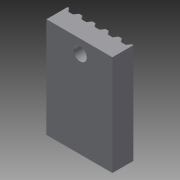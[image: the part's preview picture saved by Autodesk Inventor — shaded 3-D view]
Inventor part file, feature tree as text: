
AUTODESK INVENTOR PART (.ipt)
format: ipt  version: 2015 SP1 (Build 190203100, 203)  size: 166,912 bytes
history: native  units: in
note: dims shown in document units (in); Inventor stores cm internally (conversion verified against a paired STEP export)
features: extrude x4, sketch x4, projected_geometry x1
ambient origin geometry x8: Origin, YZ Plane, XZ Plane, XY Plane, X Axis, Y Axis, Z Axis, Center Point
bodies: Body1 (feature_tree)
feature tree (9):
  extrude  "Extrusion2"  Depth=0.1575in TaperAngle=0.0deg
  extrude  "Extrusion3"  Depth=0.0079in
  extrude  "Extrusion4"  Depth=0.3937in
  sketch  "Sketch5"  dims[d23=0.3937in d24=0.0in]
  extrude  "Extrusion5"  [1 undecoded]
  sketch  "Sketch1"  dims[d2=0.1575in d3=0.0in d4=0.1575in d5=0.0in]
  sketch  "Sketch2"  dims[d11=0.0118in d12=0.0079in d13=0.0079in d14=0.0984in d16=0.0394in]
  projected_geometry  "Projected Loop1"
  sketch  "Sketch4"  dims[d17=0.3937in d18=0.0in d19=0.0984in]
note: 1 required parameter value undecoded (feature->parameter linkage not recoverable at this tier; creation-order binding heuristic only, values carry confidence <= 0.55)
